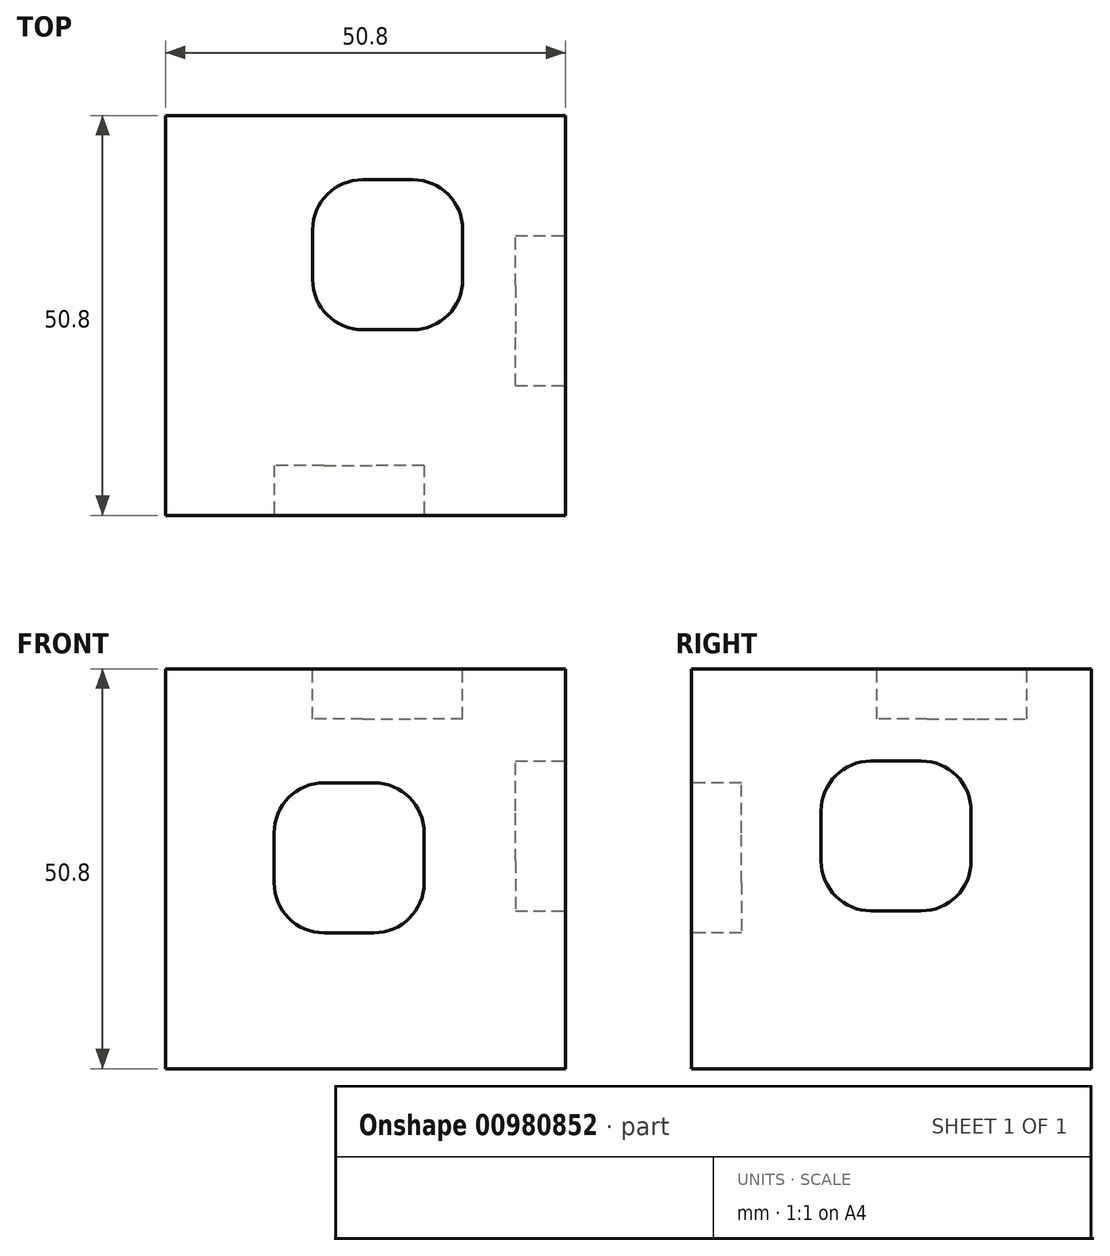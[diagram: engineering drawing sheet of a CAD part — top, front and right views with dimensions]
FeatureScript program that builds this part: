
annotation { "Feature Type Name" : "Feature", "Feature Type Description" : "" }
export const myFeature = defineFeature(function(context is Context, id is Id, definition is map)
    precondition{}
    {
        {
            var Q0;
            Q0=qCreatedBy(makeId("Top.planeOp"),FACE);
            var sketch = newSketch(context, id + "F0", { "sketchPlane" : qUnion([Q0])});
            skLineSegment(sketch, "E0.bottom", {"start": v(0, 0) * mm, "end": v(50.8, 0) * mm});
            skLineSegment(sketch, "E0.top", {"start": v(0, 50.8) * mm, "end": v(50.8, 50.8) * mm});
            skLineSegment(sketch, "E0.left", {"start": v(0, 0) * mm, "end": v(0, 50.8) * mm});
            skLineSegment(sketch, "E0.right", {"start": v(50.8, 0) * mm, "end": v(50.8, 50.8) * mm});
            skSolve(sketch);
        }
        {
            var Q0;
            Q0=makeQuery(id+"F0.imprint","IMPRINT",FACE,{"disambiguationData":[TD([[makeQuery(id+"F0.imprint","IMPRINT",EDGE,{"derivedFrom":sQuery(id+"F0.wireOp",EDGE,"E0.bottom")}),1.0]])]});
            extrude(context, id + "F1", {"entities" : qUnion([Q0]), "depth" : 50.8 * mm, "offsetDistance" : 25.4 * mm});
        }
        {
            var Q0;
            Q0=makeQuery(id+"F1.opExtrude","CAP_FACE",FACE,{"disambiguationData":[OSD([sQuery(id+"F0.wireOp",EDGE,"E0.bottom"),sQuery(id+"F0.wireOp",EDGE,"E0.top"),sQuery(id+"F0.wireOp",EDGE,"E0.left"),sQuery(id+"F0.wireOp",EDGE,"E0.right")])],"isStart":false});
            var sketch = newSketch(context, id + "F2", { "sketchPlane" : qUnion([Q0])});
            skLineSegment(sketch, "E1.bottom", {"start": v(25.04, 23.58) * mm, "end": v(31.4, 23.58) * mm});
            skLineSegment(sketch, "E1.top", {"start": v(25.04, 42.63) * mm, "end": v(31.4, 42.63) * mm});
            skLineSegment(sketch, "E1.left", {"start": v(18.7, 29.93) * mm, "end": v(18.7, 36.28) * mm});
            skLineSegment(sketch, "E1.right", {"start": v(37.74, 29.93) * mm, "end": v(37.74, 36.28) * mm});
            skPoint(sketch, "E2.visualSharp", {"position": v(18.7, 42.63) * mm});
            skArc(sketch, "E2.filletArc", {"start": v(25.04, 42.63) * mm, "mid": v(20.55, 40.77) * mm, "end": v(18.7, 36.28) * mm});
            skPoint(sketch, "E3.visualSharp", {"position": v(37.74, 23.58) * mm});
            skArc(sketch, "E3.filletArc", {"start": v(31.4, 23.58) * mm, "mid": v(35.88, 25.44) * mm, "end": v(37.74, 29.93) * mm});
            skPoint(sketch, "E4.visualSharp", {"position": v(37.74, 42.63) * mm});
            skArc(sketch, "E4.filletArc", {"start": v(37.74, 36.28) * mm, "mid": v(35.88, 40.77) * mm, "end": v(31.4, 42.63) * mm});
            skPoint(sketch, "E5.visualSharp", {"position": v(18.7, 23.58) * mm});
            skArc(sketch, "E5.filletArc", {"start": v(18.7, 29.93) * mm, "mid": v(20.55, 25.44) * mm, "end": v(25.04, 23.58) * mm});
            skSolve(sketch);
        }
        {
            var Q0;
            Q0 = qSketchRegion(id + "F2", true);
            extrude(context, id + "F3", {"entities" : qUnion([Q0]), "operationType" : NewBodyOperationType.REMOVE, "oppositeDirection" : true, "depth" : 6.35 * mm, "offsetDistance" : 25.4 * mm});
        }
        {
            var Q0;
            Q0=makeQuery(id+"F1.opExtrude","SWEPT_FACE",FACE,{"disambiguationData":[OSD([sQuery(id+"F0.wireOp",EDGE,"E0.bottom")])]});
            var sketch = newSketch(context, id + "F4", { "sketchPlane" : qUnion([Q0])});
            skLineSegment(sketch, "E6.bottom", {"start": v(20.13, 17.26) * mm, "end": v(26.48, 17.26) * mm});
            skLineSegment(sketch, "E6.top", {"start": v(20.13, 36.3) * mm, "end": v(26.48, 36.3) * mm});
            skLineSegment(sketch, "E6.left", {"start": v(13.78, 23.6) * mm, "end": v(13.78, 29.96) * mm});
            skLineSegment(sketch, "E6.right", {"start": v(32.83, 23.6) * mm, "end": v(32.83, 29.96) * mm});
            skPoint(sketch, "E7.visualSharp", {"position": v(13.78, 36.3) * mm});
            skArc(sketch, "E7.filletArc", {"start": v(20.13, 36.3) * mm, "mid": v(15.64, 34.45) * mm, "end": v(13.78, 29.96) * mm});
            skPoint(sketch, "E8.visualSharp", {"position": v(32.83, 36.3) * mm});
            skArc(sketch, "E8.filletArc", {"start": v(32.83, 29.96) * mm, "mid": v(30.97, 34.45) * mm, "end": v(26.48, 36.3) * mm});
            skPoint(sketch, "E9.visualSharp", {"position": v(32.83, 17.26) * mm});
            skArc(sketch, "E9.filletArc", {"start": v(26.48, 17.26) * mm, "mid": v(30.97, 19.12) * mm, "end": v(32.83, 23.6) * mm});
            skPoint(sketch, "E10.visualSharp", {"position": v(13.78, 17.26) * mm});
            skArc(sketch, "E10.filletArc", {"start": v(13.78, 23.6) * mm, "mid": v(15.64, 19.12) * mm, "end": v(20.13, 17.26) * mm});
            skSolve(sketch);
        }
        {
            var Q0;
            Q0 = qSketchRegion(id + "F4", true);
            extrude(context, id + "F5", {"entities" : qUnion([Q0]), "operationType" : NewBodyOperationType.REMOVE, "oppositeDirection" : true, "depth" : 6.35 * mm, "offsetDistance" : 25.4 * mm});
        }
        {
            var Q0;
            Q0=makeQuery(id+"F1.opExtrude","SWEPT_FACE",FACE,{"disambiguationData":[OSD([sQuery(id+"F0.wireOp",EDGE,"E0.right")])]});
            var sketch = newSketch(context, id + "F6", { "sketchPlane" : qUnion([Q0])});
            skLineSegment(sketch, "E11.bottom", {"start": v(29.18, 20.04) * mm, "end": v(22.83, 20.04) * mm});
            skLineSegment(sketch, "E11.top", {"start": v(29.18, 39.1) * mm, "end": v(22.83, 39.1) * mm});
            skLineSegment(sketch, "E11.left", {"start": v(35.53, 26.4) * mm, "end": v(35.53, 32.74) * mm});
            skLineSegment(sketch, "E11.right", {"start": v(16.48, 26.4) * mm, "end": v(16.48, 32.74) * mm});
            skPoint(sketch, "E12.visualSharp", {"position": v(35.53, 20.04) * mm});
            skArc(sketch, "E12.filletArc", {"start": v(29.18, 20.04) * mm, "mid": v(33.67, 21.9) * mm, "end": v(35.53, 26.4) * mm});
            skPoint(sketch, "E13.visualSharp", {"position": v(16.48, 20.04) * mm});
            skArc(sketch, "E13.filletArc", {"start": v(16.48, 26.4) * mm, "mid": v(18.34, 21.9) * mm, "end": v(22.83, 20.04) * mm});
            skPoint(sketch, "E14.visualSharp", {"position": v(16.48, 39.1) * mm});
            skArc(sketch, "E14.filletArc", {"start": v(22.83, 39.1) * mm, "mid": v(18.34, 37.23) * mm, "end": v(16.48, 32.74) * mm});
            skPoint(sketch, "E15.visualSharp", {"position": v(35.53, 39.1) * mm});
            skArc(sketch, "E15.filletArc", {"start": v(35.53, 32.74) * mm, "mid": v(33.67, 37.23) * mm, "end": v(29.18, 39.1) * mm});
            skSolve(sketch);
        }
        {
            var Q0;
            Q0 = qSketchRegion(id + "F6", true);
            extrude(context, id + "F7", {"entities" : qUnion([Q0]), "operationType" : NewBodyOperationType.REMOVE, "oppositeDirection" : true, "depth" : 6.35 * mm, "offsetDistance" : 25.4 * mm});
        }
    });
